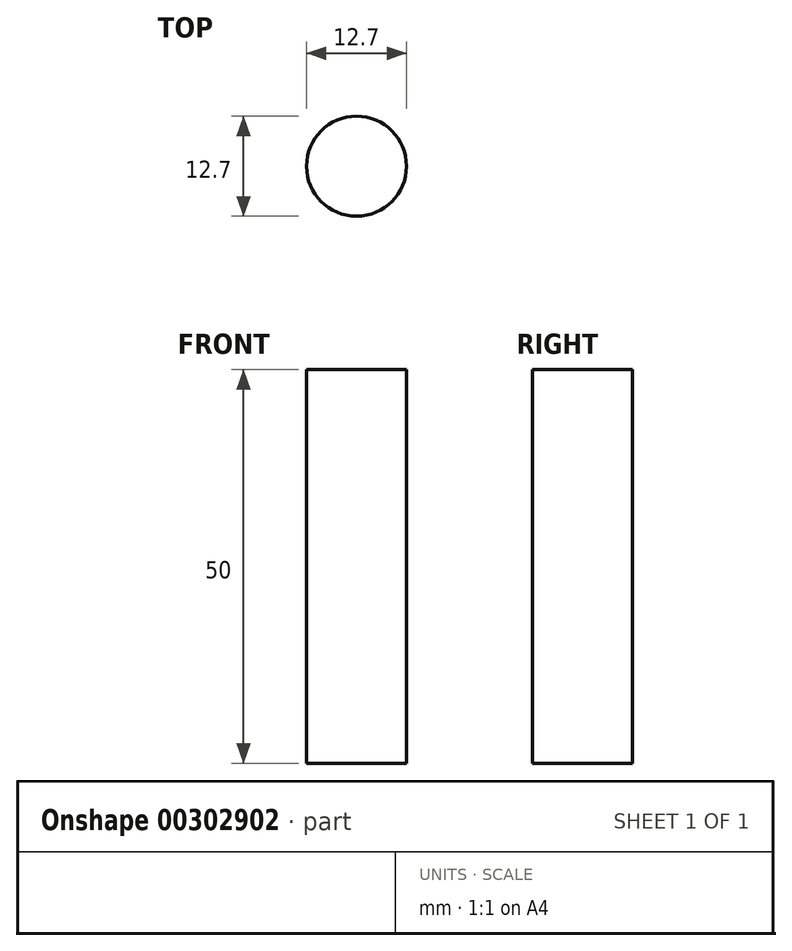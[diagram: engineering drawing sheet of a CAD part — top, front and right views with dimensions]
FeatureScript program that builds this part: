
annotation { "Feature Type Name" : "Feature", "Feature Type Description" : "" }
export const myFeature = defineFeature(function(context is Context, id is Id, definition is map)
    precondition{}
    {
        {
            var Q0;
            Q0=qCreatedBy(makeId("Top.planeOp"),FACE);
            var sketch = newSketch(context, id + "F0", { "sketchPlane" : qUnion([Q0])});
            skCircle(sketch, "E0", {"center": v(0, 0) * mm, "radius": 6.35 * mm});
            skSolve(sketch);
        }
        {
            var Q0;
            Q0=makeQuery(id+"F0.imprint","IMPRINT",FACE,{"disambiguationData":[TD([[makeQuery(id+"F0.imprint","IMPRINT",EDGE,{"derivedFrom":sQuery(id+"F0.wireOp",EDGE,"E0")}),1.0]])]});
            extrude(context, id + "F1", {"entities" : qUnion([Q0]), "depth" : 50 * mm});
        }
    });
